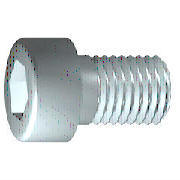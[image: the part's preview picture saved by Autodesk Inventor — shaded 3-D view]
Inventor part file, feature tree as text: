
AUTODESK INVENTOR PART (.ipt)
format: ipt  version: 2018 (Build 220112000, 112)  size: 188,928 bytes
history: native  units: mm (DEFAULTED — no unit token found)
features: sketch x2, extrude x1, plane x1, fillet x1
ambient origin geometry x7: Origin, YZ Plane, XY Plane, X Axis, Y Axis, Z Axis, Center Point
bodies: Solid1 (feature_tree), Body (feature_tree)
feature tree (5):
  extrude  "Slot"  Depth=2.5mm
  plane  "Work Plane1"
  fillet  "Fillet2"  Radius=2.5mm
  sketch  "Sketch1"  dims[d1=8.823947mm d2=0.276153mm d3=2.5mm]
  sketch  "Sketch2"  dims[d4=1.25mm d5=60.0deg d6=2.5mm d7=2.5mm d8=2.309401mm d9=4.5mm d10=90.0deg d11=10.0mm d12=0.0mm d13=8.823947mm d14=0.0mm d15=0.276052mm d16=0.276053mm d17=0.25mm d19=0.0mm d26=10.0mm d27=45.0deg d28=0.0mm d29=0.0mm d30=0.1mm]
